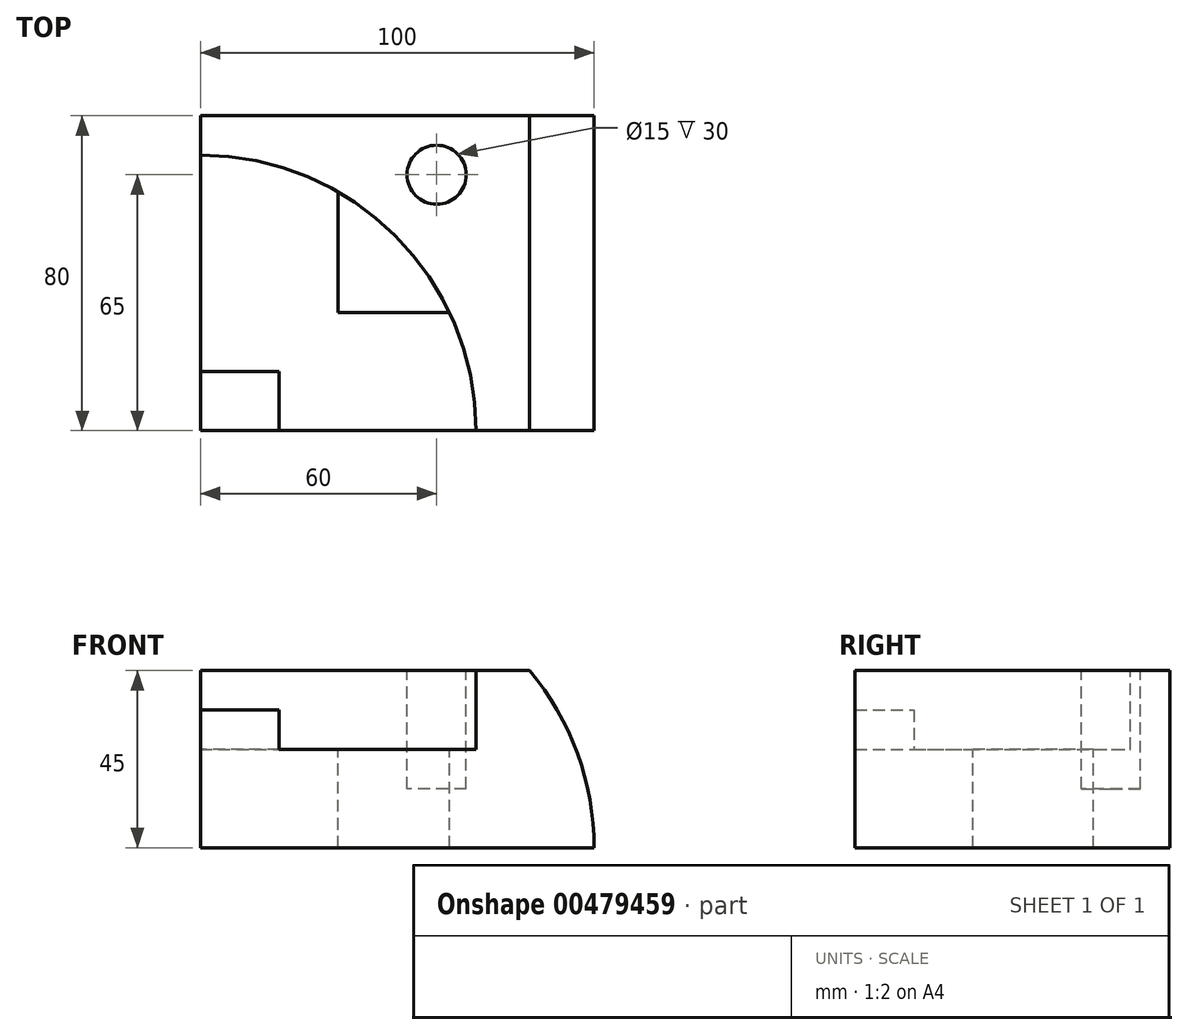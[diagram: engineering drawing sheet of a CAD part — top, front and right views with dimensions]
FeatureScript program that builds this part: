
annotation { "Feature Type Name" : "Feature", "Feature Type Description" : "" }
export const myFeature = defineFeature(function(context is Context, id is Id, definition is map)
    precondition{}
    {
        {
            var Q0;
            Q0=qCreatedBy(makeId("Front.planeOp"),FACE);
            var sketch = newSketch(context, id + "F0", { "sketchPlane" : qUnion([Q0])});
            skLineSegment(sketch, "E0.bottom", {"start": v(0, 0) * mm, "end": v(100, 0) * mm});
            skLineSegment(sketch, "E0.top", {"start": v(0, 45) * mm, "end": v(100, 45) * mm});
            skLineSegment(sketch, "E0.left", {"start": v(0, 0) * mm, "end": v(0, 45) * mm});
            skLineSegment(sketch, "E0.right", {"start": v(100, 0) * mm, "end": v(100, 45) * mm});
            skSolve(sketch);
        }
        {
            var Q0;
            Q0 = qSketchRegion(id + "F0", true);
            extrude(context, id + "F1", {"entities" : qUnion([Q0]), "depth" : 80 * mm});
        }
        {
            var Q0;
            Q0=makeQuery(id+"F1.opExtrude","SWEPT_FACE",FACE,{"disambiguationData":[OSD([sQuery(id+"F0.wireOp",EDGE,"E0.top")])]});
            var sketch = newSketch(context, id + "F2", { "sketchPlane" : qUnion([Q0])});
            skCircle(sketch, "E1", {"center": v(0, -80) * mm, "radius": 70 * mm});
            skSolve(sketch);
        }
        {
            var Q0;
            Q0 = qSketchRegion(id + "F2", true);
            extrude(context, id + "F3", {"entities" : qUnion([Q0]), "operationType" : NewBodyOperationType.REMOVE, "oppositeDirection" : true, "depth" : 20 * mm});
        }
        {
            var Q0;
            Q0=makeQuery(id+"F3.boolean.opBoolean","COPY",FACE,{"derivedFrom":makeQuery(id+"F3.opExtrude","CAP_FACE",FACE,{"disambiguationData":[OSD([sQuery(id+"F2.wireOp",EDGE,"E1")])],"isStart":false})});
            var sketch = newSketch(context, id + "F4", { "sketchPlane" : qUnion([Q0])});
            skLineSegment(sketch, "E2", {"start": v(35, -19.38) * mm, "end": v(35, -50) * mm});
            skLineSegment(sketch, "E3", {"start": v(35, -50) * mm, "end": v(63.25, -50) * mm});
            skSolve(sketch);
        }
        {
            var Q0;
            Q0 = qSketchRegion(id + "F4", true);
            var Q1;
            {var subQ0=sQuery(id+"F4.wireOp",EDGE,"E2");Q1=makeQuery(id+"F4.imprint","IMPRINT",FACE,{"disambiguationData":[TD([[makeQuery(id+"F4.imprint","IMPRINT",EDGE,{"derivedFrom":subQ0}),1.0]])]});}
            extrude(context, id + "F5", {"entities" : qUnion([Q0, Q1]), "operationType" : NewBodyOperationType.REMOVE, "endBound" : BoundingType.THROUGH_ALL, "oppositeDirection" : true, "depth" : 25 * mm});
        }
        {
            var Q0;
            Q0=makeQuery(id+"F3.boolean.opBoolean","COPY",FACE,{"derivedFrom":makeQuery(id+"F3.opExtrude","CAP_FACE",FACE,{"disambiguationData":[OSD([sQuery(id+"F2.wireOp",EDGE,"E1")])],"isStart":false})});
            var sketch = newSketch(context, id + "F6", { "sketchPlane" : qUnion([Q0])});
            skLineSegment(sketch, "E4.bottom", {"start": v(0, -80) * mm, "end": v(20, -80) * mm});
            skLineSegment(sketch, "E4.top", {"start": v(0, -65) * mm, "end": v(20, -65) * mm});
            skLineSegment(sketch, "E4.left", {"start": v(0, -80) * mm, "end": v(0, -65) * mm});
            skLineSegment(sketch, "E4.right", {"start": v(20, -80) * mm, "end": v(20, -65) * mm});
            skSolve(sketch);
        }
        {
            var Q0;
            Q0 = qSketchRegion(id + "F6", true);
            extrude(context, id + "F7", {"entities" : qUnion([Q0]), "operationType" : NewBodyOperationType.ADD, "depth" : 10 * mm});
        }
        {
            var Q0;
            Q0=makeQuery(id+"F1.opExtrude","SWEPT_FACE",FACE,{"disambiguationData":[OSD([sQuery(id+"F0.wireOp",EDGE,"E0.top")])]});
            var sketch = newSketch(context, id + "F8", { "sketchPlane" : qUnion([Q0])});
            skCircle(sketch, "E5", {"center": v(60, -15) * mm, "radius": 7.5 * mm});
            skSolve(sketch);
        }
        {
            var Q0;
            Q0 = qSketchRegion(id + "F8", true);
            extrude(context, id + "F9", {"entities" : qUnion([Q0]), "operationType" : NewBodyOperationType.REMOVE, "oppositeDirection" : true, "depth" : 30 * mm});
        }
        {
            var Q0;
            Q0=makeQuery(id+"F7.boolean.opBoolean","MERGE",FACE,{"derivedFrom":[makeQuery(id+"F1.opExtrude","CAP_FACE",FACE,{"disambiguationData":[OSD([sQuery(id+"F0.wireOp",EDGE,"E0.bottom"),sQuery(id+"F0.wireOp",EDGE,"E0.top"),sQuery(id+"F0.wireOp",EDGE,"E0.left"),sQuery(id+"F0.wireOp",EDGE,"E0.right")])],"isStart":false}),makeQuery(id+"F7.opExtrude","SWEPT_FACE",FACE,{"disambiguationData":[OSD([sQuery(id+"F6.wireOp",EDGE,"E4.bottom")])]})]});
            var sketch = newSketch(context, id + "F10", { "sketchPlane" : qUnion([Q0])});
            skArc(sketch, "E6", {"start": v(100, 0) * mm, "mid": v(95.78, 23.94) * mm, "end": v(83.62, 45) * mm});
            skSolve(sketch);
        }
        {
            var Q0;
            Q0 = qSketchRegion(id + "F10", true);
            var Q1;
            {var subQ0=sQuery(id+"F10.wireOp",EDGE,"E6");Q1=makeQuery(id+"F10.imprint","IMPRINT",FACE,{"disambiguationData":[TD([[makeQuery(id+"F10.imprint","IMPRINT",EDGE,{"derivedFrom":subQ0}),-1.0]])]});}
            extrude(context, id + "F11", {"entities" : qUnion([Q0, Q1]), "operationType" : NewBodyOperationType.REMOVE, "endBound" : BoundingType.THROUGH_ALL, "oppositeDirection" : true, "depth" : 25 * mm});
        }
    });
